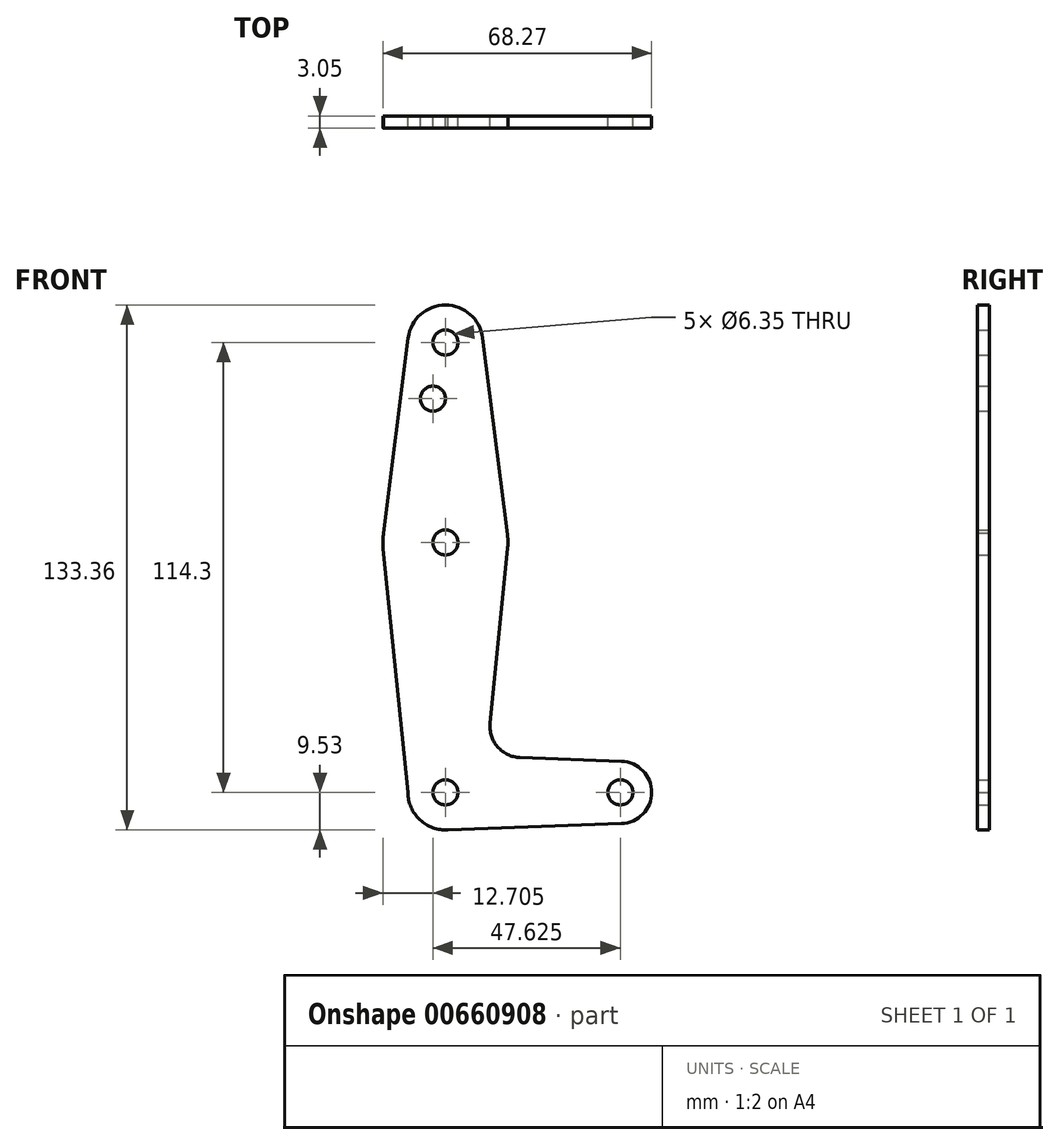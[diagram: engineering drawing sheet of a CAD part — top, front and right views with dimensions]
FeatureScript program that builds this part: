
annotation { "Feature Type Name" : "Feature", "Feature Type Description" : "" }
export const myFeature = defineFeature(function(context is Context, id is Id, definition is map)
    precondition{}
    {
        {
            var Q0;
            Q0=qCreatedBy(makeId("Front.planeOp"),FACE);
            var sketch = newSketch(context, id + "F0", { "sketchPlane" : qUnion([Q0])});
            skLineSegment(sketch, "E0", {"start": v(0, 0) * mm, "end": v(44.45, 0) * mm, "construction": true});
            skCircle(sketch, "E1", {"center": v(0, 0) * mm, "radius": 9.53 * mm});
            skCircle(sketch, "E2", {"center": v(44.45, 0) * mm, "radius": 7.94 * mm});
            skLineSegment(sketch, "E3", {"start": v(0, 0) * mm, "end": v(0, 114.3) * mm, "construction": true});
            skCircle(sketch, "E4", {"center": v(0, 114.3) * mm, "radius": 9.53 * mm});
            skCircle(sketch, "E5", {"center": v(0, 63.5) * mm, "radius": 15.88 * mm});
            skLineSegment(sketch, "E6", {"start": v(-9.53, 0) * mm, "end": v(-15.8, 61.9) * mm});
            skLineSegment(sketch, "E7", {"start": v(-15.8, 65.1) * mm, "end": v(-9.45, 115.49) * mm});
            skLineSegment(sketch, "E8", {"start": v(0, -9.53) * mm, "end": v(44.73, -7.93) * mm});
            skCircle(sketch, "E9", {"center": v(0, 114.3) * mm, "radius": 3.18 * mm});
            skCircle(sketch, "E10", {"center": v(0, 63.5) * mm, "radius": 3.18 * mm});
            skCircle(sketch, "E11", {"center": v(0, 0) * mm, "radius": 3.18 * mm});
            skCircle(sketch, "E12", {"center": v(44.45, 0) * mm, "radius": 3.18 * mm});
            skLineSegment(sketch, "E13", {"start": v(9.45, 115.5) * mm, "end": v(15.75, 65.48) * mm});
            skLineSegment(sketch, "E14", {"start": v(15.8, 61.91) * mm, "end": v(11.34, 17.6) * mm});
            skLineSegment(sketch, "E15", {"start": v(18.97, 8.85) * mm, "end": v(44.73, 7.93) * mm});
            skArc(sketch, "E16.filletArc", {"start": v(11.34, 17.6) * mm, "mid": v(13.26, 11.57) * mm, "end": v(18.97, 8.85) * mm});
            skCircle(sketch, "E17", {"center": v(-3.18, 100.03) * mm, "radius": 3.18 * mm});
            skSolve(sketch);
        }
        {
            var Q0;
            Q0 = qSketchRegion(id + "F0", true);
            extrude(context, id + "F1", {"entities" : qUnion([Q0]), "depth" : 3.05 * mm, "offsetDistance" : 25.4 * mm});
        }
    });
